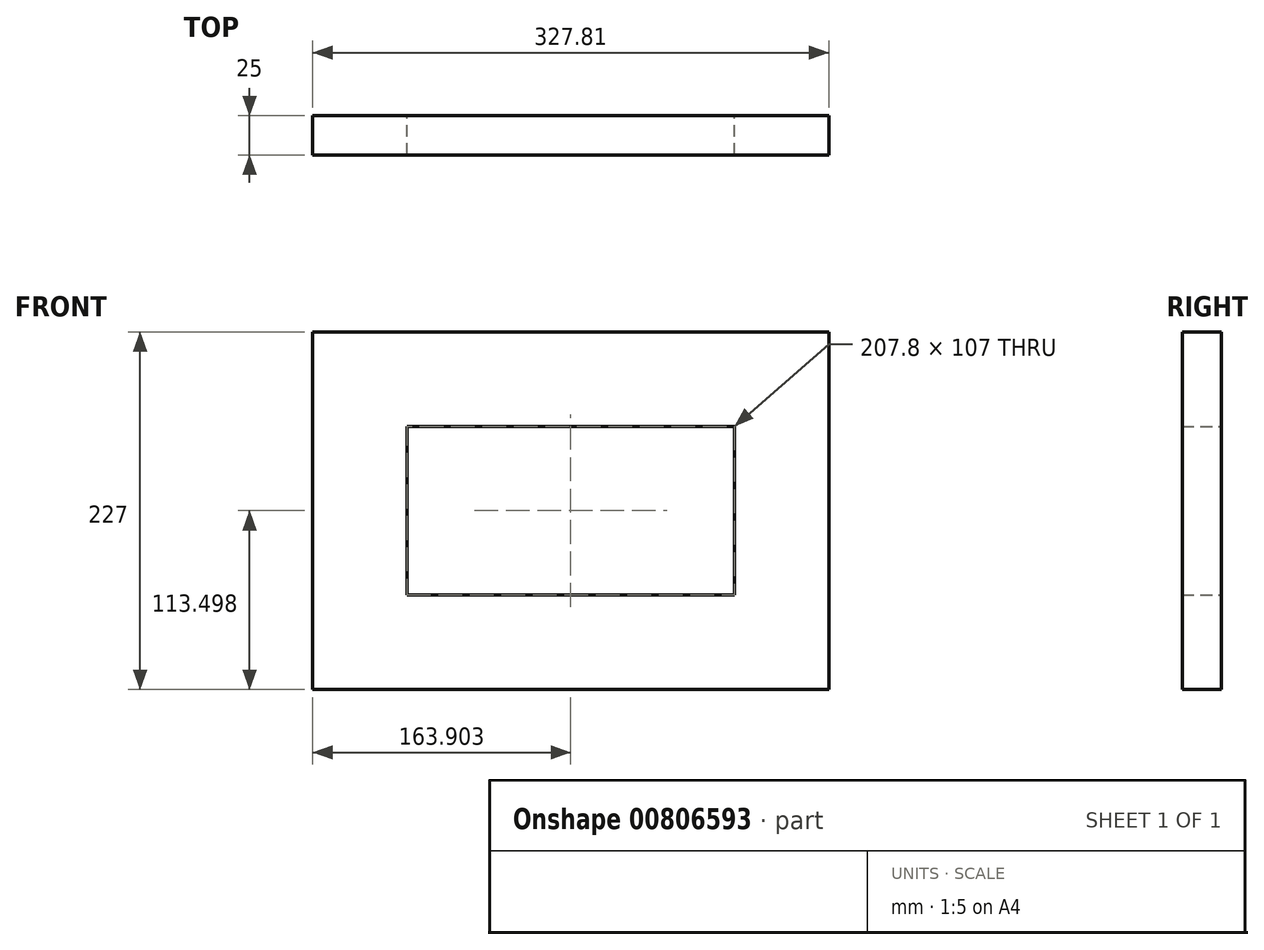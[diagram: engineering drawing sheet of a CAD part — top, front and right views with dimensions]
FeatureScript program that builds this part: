
annotation { "Feature Type Name" : "Feature", "Feature Type Description" : "" }
export const myFeature = defineFeature(function(context is Context, id is Id, definition is map)
    precondition{}
    {
        {
            var Q0;
            Q0=qCreatedBy(makeId("Front.planeOp"),FACE);
            var sketch = newSketch(context, id + "F0", { "sketchPlane" : qUnion([Q0])});
            skLineSegment(sketch, "E0.bottom", {"start": v(-93.77, 48.87) * mm, "end": v(114.04, 48.87) * mm});
            skLineSegment(sketch, "E0.top", {"start": v(-93.77, -58.13) * mm, "end": v(114.04, -58.13) * mm});
            skLineSegment(sketch, "E0.left", {"start": v(-93.77, 48.87) * mm, "end": v(-93.77, -58.13) * mm});
            skLineSegment(sketch, "E0.right", {"start": v(114.04, 48.87) * mm, "end": v(114.04, -58.13) * mm});
            skLineSegment(sketch, "E1.0", {"start": v(-153.77, 108.87) * mm, "end": v(174.04, 108.87) * mm});
            skLineSegment(sketch, "E1.1", {"start": v(-153.77, 108.87) * mm, "end": v(-153.77, -118.13) * mm});
            skLineSegment(sketch, "E1.2", {"start": v(-153.77, -118.13) * mm, "end": v(174.04, -118.13) * mm});
            skLineSegment(sketch, "E1.3", {"start": v(174.04, 108.87) * mm, "end": v(174.04, -118.13) * mm});
            skSolve(sketch);
        }
        {
            var Q0;
            Q0 = qSketchRegion(id + "F0", true);
            extrude(context, id + "F1", {"entities" : qUnion([Q0]), "depth" : 25 * mm, "offsetDistance" : 25 * mm});
        }
    });
